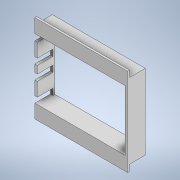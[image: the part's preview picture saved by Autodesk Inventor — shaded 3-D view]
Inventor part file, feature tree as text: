
AUTODESK INVENTOR PART (.ipt)
format: ipt  version: 2020.2 (Build 242310000, 310)  size: 194,560 bytes
history: native  units: mm
features: extrude x5, sketch x5
ambient origin geometry x8: Origin, YZ Plane, XZ Plane, XY Plane, X Axis, Y Axis, Z Axis, Center Point
bodies: Solide1 (feature_tree)
feature tree (10):
  extrude  "Extrusion1"  Depth=48.0mm
  extrude  "Extrusion3"  Depth=48.0mm
  extrude  "Extrusion4"  Depth=70.0mm
  extrude  "Extrusion5"  Depth=70.0mm
  extrude  "Extrusion6"  Depth=60.0mm
  sketch  "Esquisse1"
  sketch  "Esquisse3"
  sketch  "Esquisse4"
  sketch  "Esquisse5"
  sketch  "Esquisse6"
